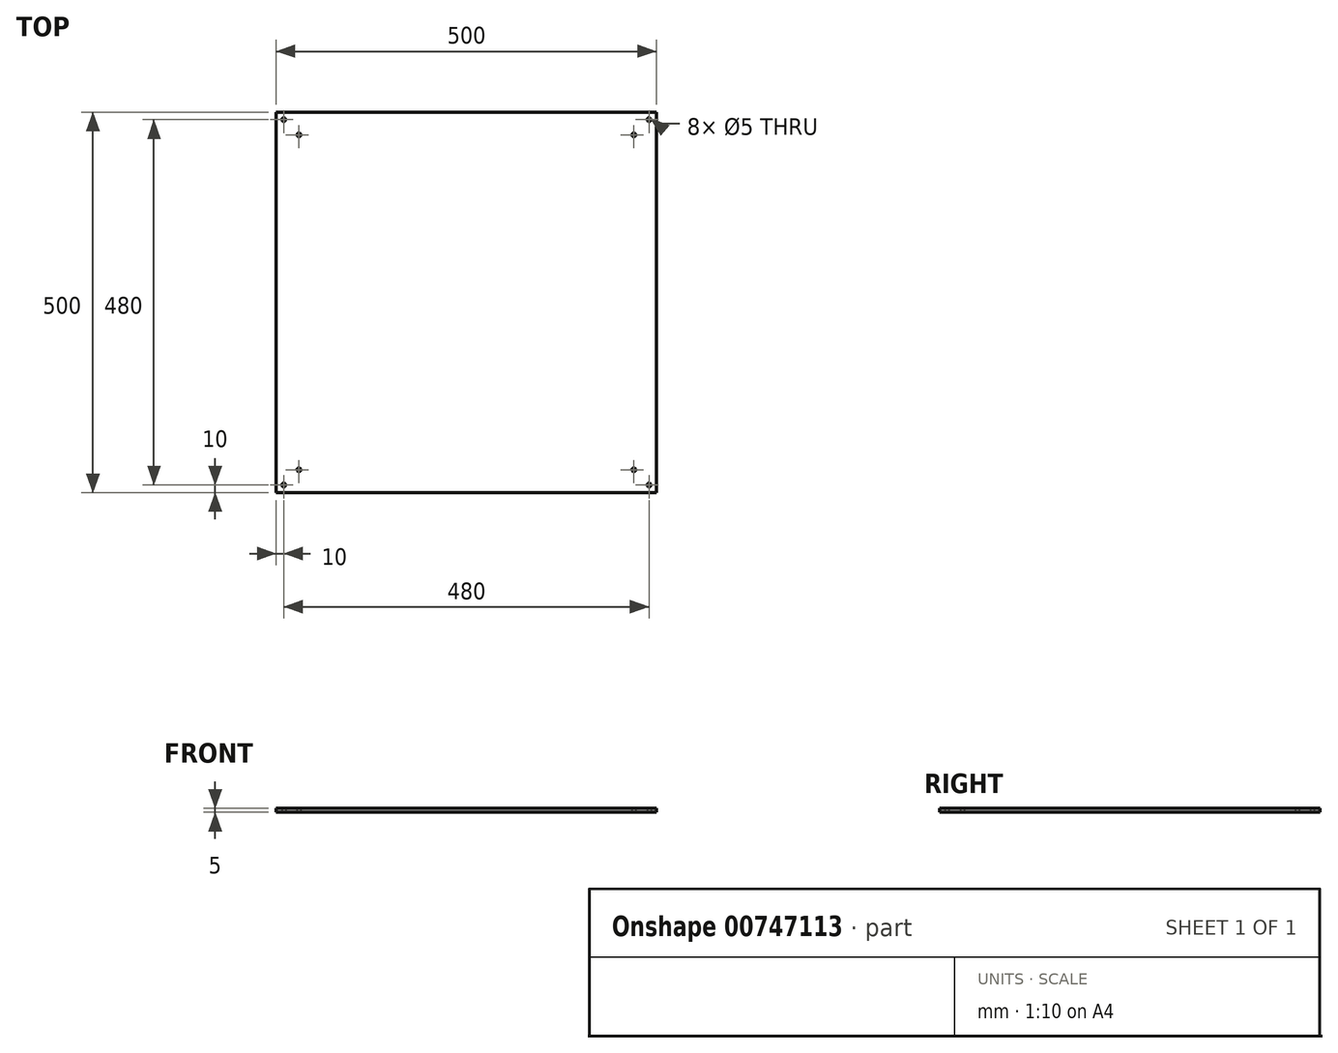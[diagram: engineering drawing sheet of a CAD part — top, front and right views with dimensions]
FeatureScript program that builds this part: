
annotation { "Feature Type Name" : "Feature", "Feature Type Description" : "" }
export const myFeature = defineFeature(function(context is Context, id is Id, definition is map)
    precondition{}
    {
        {
            var Q0;
            Q0=qCreatedBy(makeId("Top.planeOp"),FACE);
            var sketch = newSketch(context, id + "F0", { "sketchPlane" : qUnion([Q0])});
            skLineSegment(sketch, "E0.bottom", {"start": v(-250, 250) * mm, "end": v(250, 250) * mm});
            skLineSegment(sketch, "E0.top", {"start": v(-250, -250) * mm, "end": v(250, -250) * mm});
            skLineSegment(sketch, "E0.left", {"start": v(-250, 250) * mm, "end": v(-250, -250) * mm});
            skLineSegment(sketch, "E0.right", {"start": v(250, 250) * mm, "end": v(250, -250) * mm});
            skPoint(sketch, "E0.middle", {"position": v(0, 0) * mm});
            skCircle(sketch, "E1", {"center": v(-240, 240) * mm, "radius": 2.5 * mm});
            skCircle(sketch, "E2", {"center": v(-220, 220) * mm, "radius": 2.5 * mm});
            skCircle(sketch, "E3", {"center": v(240, 240) * mm, "radius": 2.5 * mm});
            skCircle(sketch, "E4", {"center": v(220, 220) * mm, "radius": 2.5 * mm});
            skCircle(sketch, "E5", {"center": v(220, -220) * mm, "radius": 2.5 * mm});
            skCircle(sketch, "E6", {"center": v(240, -240) * mm, "radius": 2.5 * mm});
            skCircle(sketch, "E7", {"center": v(-220, -220) * mm, "radius": 2.5 * mm});
            skCircle(sketch, "E8", {"center": v(-240, -240) * mm, "radius": 2.5 * mm});
            skSolve(sketch);
        }
        {
            var Q0;
            Q0=makeQuery(id+"F0.imprint","IMPRINT",FACE,{"disambiguationData":[TD([[makeQuery(id+"F0.imprint","IMPRINT",EDGE,{"derivedFrom":sQuery(id+"F0.wireOp",EDGE,"E0.bottom")}),-1.0]])]});
            extrude(context, id + "F1", {"entities" : qUnion([Q0]), "depth" : 5 * mm, "offsetDistance" : 25 * mm});
        }
    });
